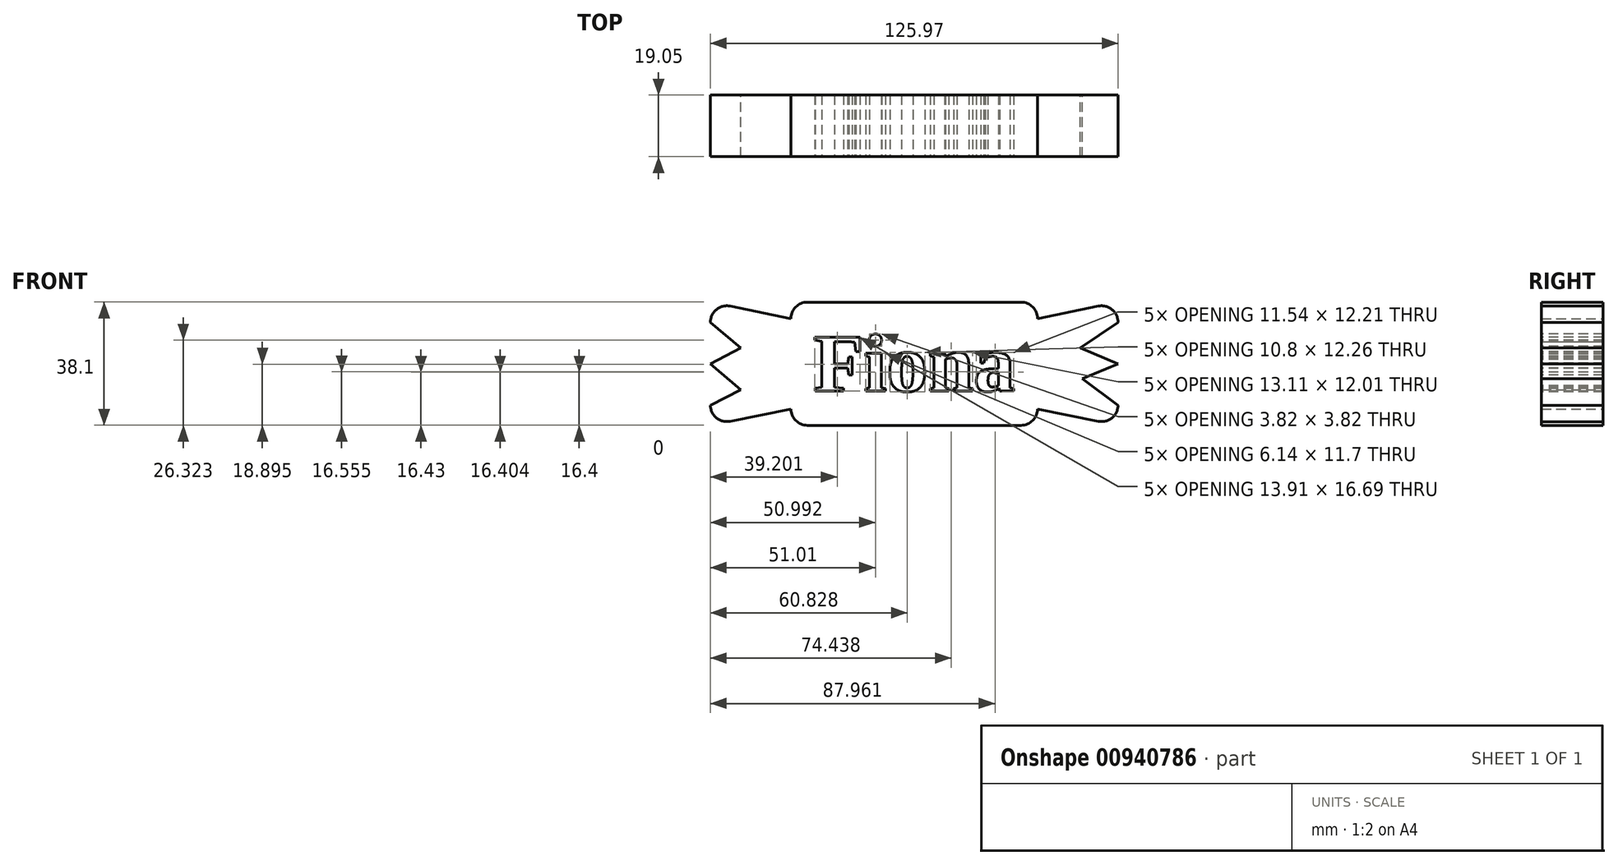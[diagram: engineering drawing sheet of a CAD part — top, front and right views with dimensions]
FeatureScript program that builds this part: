
annotation { "Feature Type Name" : "Feature", "Feature Type Description" : "" }
export const myFeature = defineFeature(function(context is Context, id is Id, definition is map)
    precondition{}
    {
        {
            var Q0;
            Q0=qCreatedBy(makeId("Front.planeOp"),FACE);
            var sketch = newSketch(context, id + "F0", { "sketchPlane" : qUnion([Q0])});
            skLineSegment(sketch, "E0.bottom", {"start": v(-28.34, 27.15) * mm, "end": v(37.7, 27.15) * mm});
            skLineSegment(sketch, "E0.top", {"start": v(-28.34, -10.95) * mm, "end": v(37.7, -10.95) * mm});
            skLineSegment(sketch, "E0.left", {"start": v(-33.42, 22.07) * mm, "end": v(-33.42, -5.87) * mm});
            skLineSegment(sketch, "E0.right", {"start": v(42.78, 22.07) * mm, "end": v(42.78, -5.87) * mm});
            skPoint(sketch, "E1.visualSharp", {"position": v(-33.42, 27.15) * mm});
            skArc(sketch, "E1.filletArc", {"start": v(-28.34, 27.15) * mm, "mid": v(-31.94, 25.66) * mm, "end": v(-33.42, 22.07) * mm});
            skPoint(sketch, "E2.visualSharp", {"position": v(42.78, 27.15) * mm});
            skArc(sketch, "E2.filletArc", {"start": v(42.78, 22.07) * mm, "mid": v(41.29, 25.66) * mm, "end": v(37.7, 27.15) * mm});
            skPoint(sketch, "E3.visualSharp", {"position": v(42.78, -10.95) * mm});
            skArc(sketch, "E3.filletArc", {"start": v(37.7, -10.95) * mm, "mid": v(41.29, -9.47) * mm, "end": v(42.78, -5.87) * mm});
            skPoint(sketch, "E4.visualSharp", {"position": v(-33.42, -10.95) * mm});
            skArc(sketch, "E4.filletArc", {"start": v(-33.42, -5.87) * mm, "mid": v(-31.94, -9.47) * mm, "end": v(-28.34, -10.95) * mm});
            skLineSegment(sketch, "E5", {"start": v(42.78, 22.07) * mm, "end": v(61.57, 25.9) * mm});
            skLineSegment(sketch, "E6", {"start": v(42.78, -5.87) * mm, "end": v(61.57, -9.7) * mm});
            skLineSegment(sketch, "E7", {"start": v(67.66, 20.92) * mm, "end": v(67.66, -4.73) * mm});
            skPoint(sketch, "E8.visualSharp", {"position": v(67.66, 27.15) * mm});
            skArc(sketch, "E8.filletArc", {"start": v(67.66, 20.92) * mm, "mid": v(65.8, 24.86) * mm, "end": v(61.57, 25.9) * mm});
            skPoint(sketch, "E9.visualSharp", {"position": v(67.66, -10.95) * mm});
            skArc(sketch, "E9.filletArc", {"start": v(61.57, -9.7) * mm, "mid": v(65.8, -8.67) * mm, "end": v(67.66, -4.73) * mm});
            skLineSegment(sketch, "E10", {"start": v(-33.42, 22.07) * mm, "end": v(-52.21, 25.9) * mm});
            skLineSegment(sketch, "E11", {"start": v(-33.42, -5.87) * mm, "end": v(-52.21, -9.7) * mm});
            skLineSegment(sketch, "E12", {"start": v(-58.3, 20.92) * mm, "end": v(-58.3, -4.73) * mm});
            skPoint(sketch, "E13.visualSharp", {"position": v(-58.3, 27.15) * mm});
            skArc(sketch, "E13.filletArc", {"start": v(-52.21, 25.9) * mm, "mid": v(-56.44, 24.86) * mm, "end": v(-58.3, 20.92) * mm});
            skPoint(sketch, "E14.visualSharp", {"position": v(-58.3, -10.95) * mm});
            skArc(sketch, "E14.filletArc", {"start": v(-58.3, -4.73) * mm, "mid": v(-56.44, -8.67) * mm, "end": v(-52.21, -9.7) * mm});
            skLineSegment(sketch, "E15", {"start": v(67.66, 20.92) * mm, "end": v(55.94, 12.96) * mm});
            skLineSegment(sketch, "E16", {"start": v(55.94, 12.96) * mm, "end": v(67.66, 8.1) * mm});
            skLineSegment(sketch, "E17", {"start": v(67.66, 8.1) * mm, "end": v(56.59, 3.47) * mm});
            skLineSegment(sketch, "E18", {"start": v(56.59, 3.47) * mm, "end": v(67.66, -4.73) * mm});
            skLineSegment(sketch, "E19", {"start": v(-58.3, 20.92) * mm, "end": v(-48.88, 12.93) * mm});
            skLineSegment(sketch, "E20", {"start": v(-48.88, 12.93) * mm, "end": v(-58.3, 8.1) * mm});
            skLineSegment(sketch, "E21", {"start": v(-58.3, 8.1) * mm, "end": v(-48.88, 0) * mm});
            skLineSegment(sketch, "E22", {"start": v(-48.88, 0) * mm, "end": v(-58.3, -4.73) * mm});
            skSolve(sketch);
        }
        {
            var Q0;
            Q0=makeQuery(id+"F0.imprint","IMPRINT",FACE,{"disambiguationData":[TD([[makeQuery(id+"F0.imprint","IMPRINT",EDGE,{"derivedFrom":sQuery(id+"F0.wireOp",EDGE,"E0.left")}),-1.0]])]});
            var Q1;
            Q1=makeQuery(id+"F0.imprint","IMPRINT",FACE,{"disambiguationData":[TD([[makeQuery(id+"F0.imprint","IMPRINT",EDGE,{"derivedFrom":sQuery(id+"F0.wireOp",EDGE,"E0.bottom")}),-1.0]])]});
            var Q2;
            Q2=makeQuery(id+"F0.imprint","IMPRINT",FACE,{"disambiguationData":[TD([[makeQuery(id+"F0.imprint","IMPRINT",EDGE,{"derivedFrom":sQuery(id+"F0.wireOp",EDGE,"E0.right")}),1.0]])]});
            extrude(context, id + "F1", {"entities" : qUnion([Q0, Q1, Q2]), "depth" : 19.05 * mm, "offsetDistance" : 25.4 * mm});
        }
        {
            var Q0;
            Q0=makeQuery(id+"F1.opExtrude","CAP_FACE",FACE,{"disambiguationData":[OSD([sQuery(id+"F0.wireOp",EDGE,"E0.bottom"),sQuery(id+"F0.wireOp",EDGE,"E0.top"),sQuery(id+"F0.wireOp",EDGE,"E1.filletArc"),sQuery(id+"F0.wireOp",EDGE,"E2.filletArc"),sQuery(id+"F0.wireOp",EDGE,"E3.filletArc"),sQuery(id+"F0.wireOp",EDGE,"E4.filletArc"),sQuery(id+"F0.wireOp",EDGE,"E5"),sQuery(id+"F0.wireOp",EDGE,"E6"),sQuery(id+"F0.wireOp",EDGE,"E8.filletArc"),sQuery(id+"F0.wireOp",EDGE,"E9.filletArc"),sQuery(id+"F0.wireOp",EDGE,"E10"),sQuery(id+"F0.wireOp",EDGE,"E11"),sQuery(id+"F0.wireOp",EDGE,"E13.filletArc"),sQuery(id+"F0.wireOp",EDGE,"E14.filletArc"),sQuery(id+"F0.wireOp",EDGE,"E15"),sQuery(id+"F0.wireOp",EDGE,"E16"),sQuery(id+"F0.wireOp",EDGE,"E17"),sQuery(id+"F0.wireOp",EDGE,"E18"),sQuery(id+"F0.wireOp",EDGE,"E19"),sQuery(id+"F0.wireOp",EDGE,"E20"),sQuery(id+"F0.wireOp",EDGE,"E21"),sQuery(id+"F0.wireOp",EDGE,"E22")])],"isStart":false});
            var sketch = newSketch(context, id + "F2", { "sketchPlane" : qUnion([Q0])});
            skText(sketch, "E23", { "text": "Fiona", "fontName": "Tinos-Bold.ttf"});
            const initialGuessF2  = {"E23": [-0.0265, -0.0004, 1, 0, 0.01835]};
            skSetInitialGuess(sketch, initialGuessF2);
            skSolve(sketch);
        }
        {
            var Q0;
            Q0 = qSketchRegion(id + "F2", true);
            extrude(context, id + "F3", {"entities" : qUnion([Q0]), "operationType" : NewBodyOperationType.REMOVE, "oppositeDirection" : true, "depth" : 44.2 * mm, "offsetDistance" : 25.4 * mm});
        }
    });
